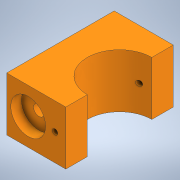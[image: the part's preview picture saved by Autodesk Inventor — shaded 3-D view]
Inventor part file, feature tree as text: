
AUTODESK INVENTOR PART (.ipt)
format: ipt  version: 2022 (Build 260153000, 153)  size: 131,584 bytes
history: native  units: mm
features: sketch x3, hole x2, extrude x1
ambient origin geometry x8: Origin, YZ Plane, XZ Plane, XY Plane, X Axis, Y Axis, Z Axis, Center Point
bodies: Solid1 (feature_tree)
feature tree (6):
  extrude  "Extrusion1"  Depth=55.0mm
  hole  "Hole1"  [1 undecoded]
  hole  "Hole2"  [1 undecoded]
  sketch  "Sketch1"  dims[d0=100.0mm d1=55.0mm]
  sketch  "Sketch2"  dims[d3=60.0mm d4=50.0mm d5=0.0mm]
  sketch  "Sketch4"  dims[d7=10.0mm d8=6.0mm d9=32.4mm d10=10.0mm d11=90.0deg d12=8.0mm d13=0.0mm d14=20.0mm d15=10.0mm d16=5.0mm d17=6.0mm d18=4.0mm d19=2.0mm d20=90.0deg d21=8.0mm d22=20.594885mm]
note: 2 required parameter values undecoded (feature->parameter linkage not recoverable at this tier; creation-order binding heuristic only, values carry confidence <= 0.55)
